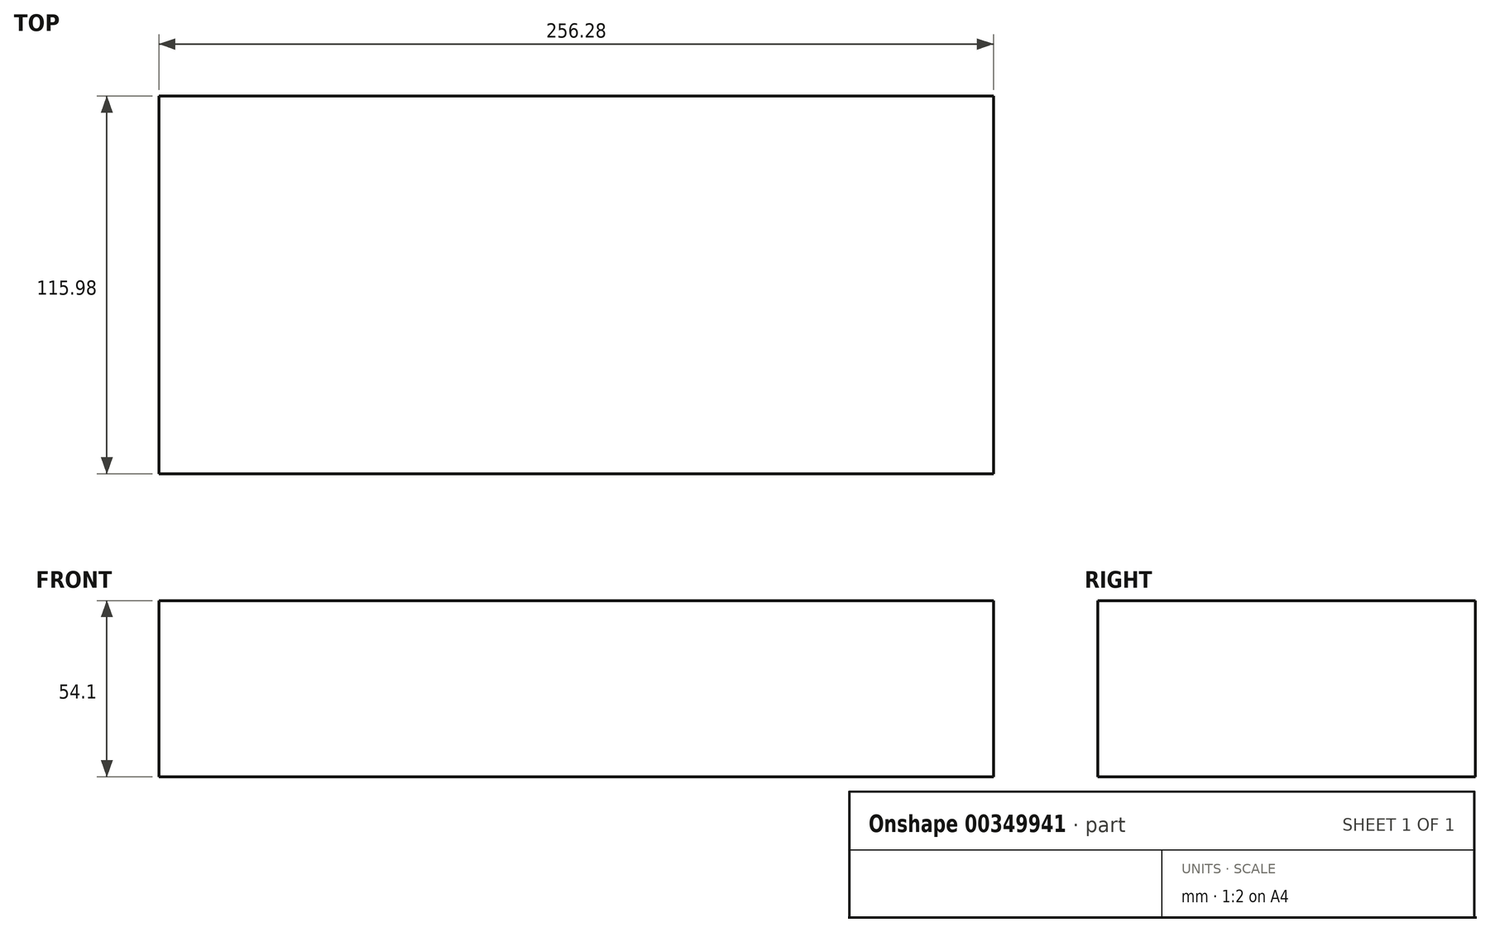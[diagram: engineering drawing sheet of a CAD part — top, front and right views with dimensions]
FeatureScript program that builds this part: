
annotation { "Feature Type Name" : "Feature", "Feature Type Description" : "" }
export const myFeature = defineFeature(function(context is Context, id is Id, definition is map)
    precondition{}
    {
        {
            var Q0;
            Q0=qCreatedBy(makeId("Top.planeOp"),FACE);
            var sketch = newSketch(context, id + "F0", { "sketchPlane" : qUnion([Q0])});
            skLineSegment(sketch, "E0.bottom", {"start": v(128.14, -58) * mm, "end": v(-128.14, -58) * mm});
            skLineSegment(sketch, "E0.top", {"start": v(128.14, 58) * mm, "end": v(-128.14, 58) * mm});
            skLineSegment(sketch, "E0.left", {"start": v(128.14, -58) * mm, "end": v(128.14, 58) * mm});
            skLineSegment(sketch, "E0.right", {"start": v(-128.14, -58) * mm, "end": v(-128.14, 58) * mm});
            skPoint(sketch, "E0.middle", {"position": v(0, 0) * mm});
            skSolve(sketch);
        }
        {
            var Q0;
            Q0 = qSketchRegion(id + "F0", true);
            extrude(context, id + "F1", {"entities" : qUnion([Q0]), "depth" : 54.1 * mm, "offsetDistance" : 25.4 * mm});
        }
    });
